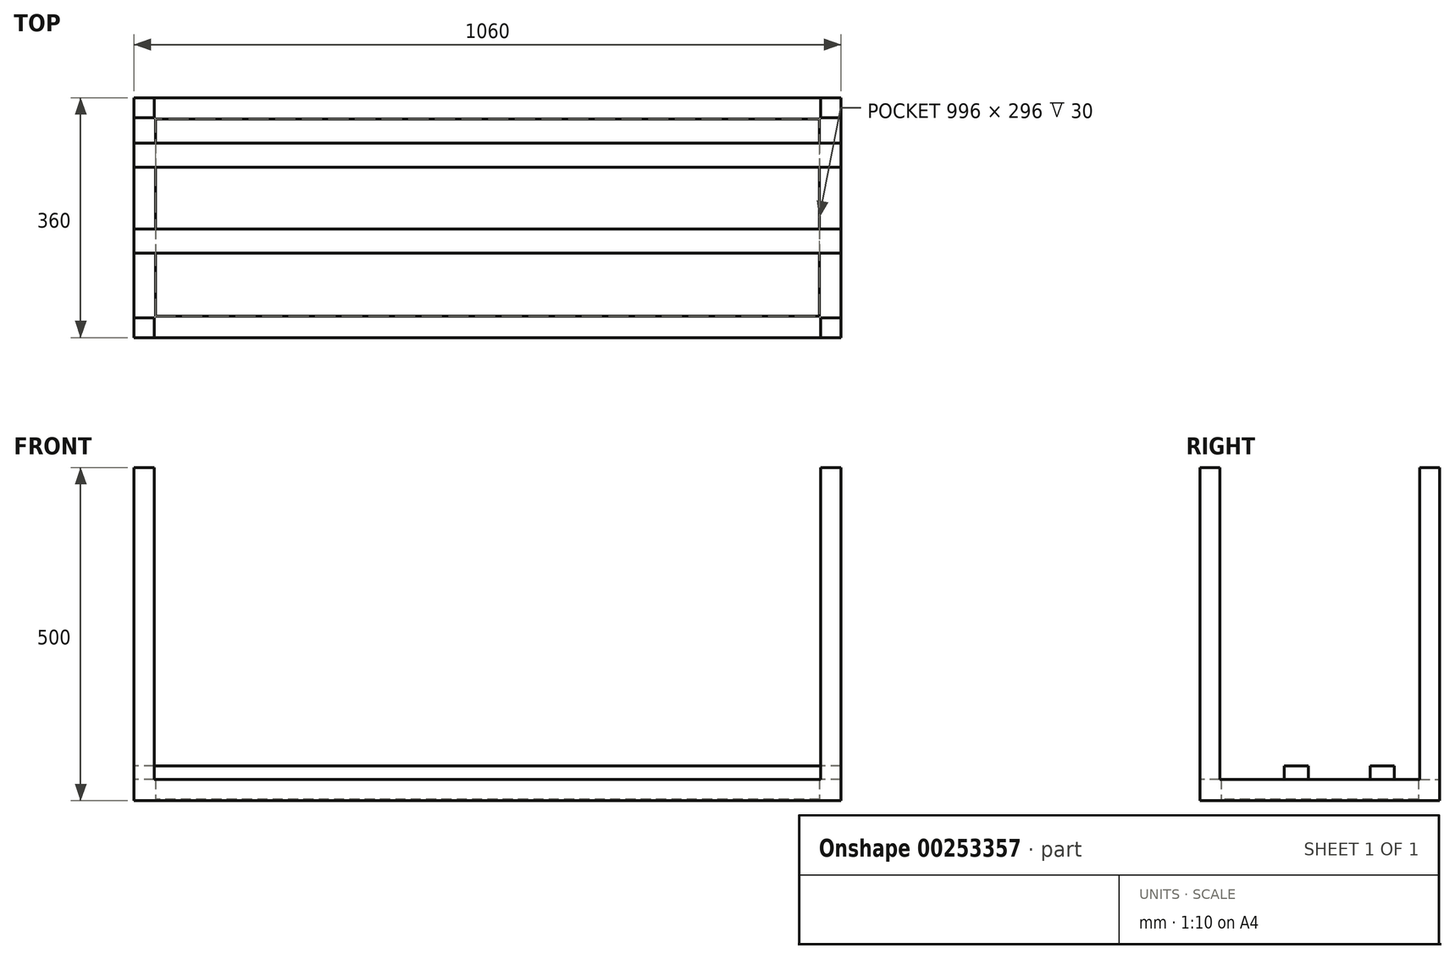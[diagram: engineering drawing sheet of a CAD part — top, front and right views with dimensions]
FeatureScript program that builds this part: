
annotation { "Feature Type Name" : "Feature", "Feature Type Description" : "" }
export const myFeature = defineFeature(function(context is Context, id is Id, definition is map)
    precondition{}
    {
        {
            var Q0;
            Q0=qCreatedBy(makeId("Top.planeOp"),FACE);
            var sketch = newSketch(context, id + "F0", { "sketchPlane" : qUnion([Q0])});
            skLineSegment(sketch, "E0.bottom", {"start": v(500, 150) * mm, "end": v(-500, 150) * mm});
            skLineSegment(sketch, "E0.top", {"start": v(500, -150) * mm, "end": v(-500, -150) * mm});
            skLineSegment(sketch, "E0.left", {"start": v(500, 150) * mm, "end": v(500, -150) * mm});
            skLineSegment(sketch, "E0.right", {"start": v(-500, 150) * mm, "end": v(-500, -150) * mm});
            skPoint(sketch, "E0.middle", {"position": v(0, 0) * mm});
            skLineSegment(sketch, "E1.bottom", {"start": v(530, 180) * mm, "end": v(-530, 180) * mm});
            skLineSegment(sketch, "E1.top", {"start": v(530, -180) * mm, "end": v(-530, -180) * mm});
            skLineSegment(sketch, "E1.left", {"start": v(530, 180) * mm, "end": v(530, -180) * mm});
            skLineSegment(sketch, "E1.right", {"start": v(-530, 180) * mm, "end": v(-530, -180) * mm});
            skLineSegment(sketch, "E2", {"start": v(-500, 150) * mm, "end": v(-500, 180) * mm});
            skLineSegment(sketch, "E3", {"start": v(-500, 150) * mm, "end": v(-530, 150) * mm});
            skLineSegment(sketch, "E4", {"start": v(-500, -150) * mm, "end": v(-530, -150) * mm});
            skLineSegment(sketch, "E5", {"start": v(-500, -150) * mm, "end": v(-500, -180) * mm});
            skLineSegment(sketch, "E6", {"start": v(500, -150) * mm, "end": v(500, -180) * mm});
            skLineSegment(sketch, "E7", {"start": v(500, -150) * mm, "end": v(530, -150) * mm});
            skLineSegment(sketch, "E8", {"start": v(500, 150) * mm, "end": v(500, 180) * mm});
            skLineSegment(sketch, "E9", {"start": v(500, 150) * mm, "end": v(530, 150) * mm});
            skSolve(sketch);
        }
        {
            var Q0;
            Q0=makeQuery(id+"F0.imprint","IMPRINT",FACE,{"disambiguationData":[TD([[makeQuery(id+"F0.imprint","IMPRINT",EDGE,{"derivedFrom":sQuery(id+"F0.wireOp",EDGE,"E0.bottom")}),-1.0]])]});
            var Q1;
            Q1=makeQuery(id+"F0.imprint","IMPRINT",FACE,{"disambiguationData":[TD([[makeQuery(id+"F0.imprint","IMPRINT",EDGE,{"derivedFrom":sQuery(id+"F0.wireOp",EDGE,"E0.right")}),-1.0]])]});
            var Q2;
            Q2=makeQuery(id+"F0.imprint","IMPRINT",FACE,{"disambiguationData":[TD([[makeQuery(id+"F0.imprint","IMPRINT",EDGE,{"derivedFrom":sQuery(id+"F0.wireOp",EDGE,"E0.top")}),1.0]])]});
            var Q3;
            Q3=makeQuery(id+"F0.imprint","IMPRINT",FACE,{"disambiguationData":[TD([[makeQuery(id+"F0.imprint","IMPRINT",EDGE,{"derivedFrom":sQuery(id+"F0.wireOp",EDGE,"E0.left")}),1.0]])]});
            extrude(context, id + "F1", {"entities" : qUnion([Q0, Q1, Q2, Q3]), "depth" : 30 * mm});
        }
        {
            var Q0;
            {var subQ3=sQuery(id+"F0.wireOp",EDGE,"E2");Q0=makeQuery(id+"F0.imprint","IMPRINT",FACE,{"disambiguationData":[TD([[makeQuery(id+"F0.imprint","IMPRINT",EDGE,{"derivedFrom":subQ3}),1.0]])]});}
            var Q1;
            {var subQ4=sQuery(id+"F0.wireOp",EDGE,"E4");Q1=makeQuery(id+"F0.imprint","IMPRINT",FACE,{"disambiguationData":[TD([[makeQuery(id+"F0.imprint","IMPRINT",EDGE,{"derivedFrom":subQ4}),1.0]])]});}
            var Q2;
            {var subQ3=sQuery(id+"F0.wireOp",EDGE,"E6");Q2=makeQuery(id+"F0.imprint","IMPRINT",FACE,{"disambiguationData":[TD([[makeQuery(id+"F0.imprint","IMPRINT",EDGE,{"derivedFrom":subQ3}),1.0]])]});}
            var Q3;
            {var subQ3=sQuery(id+"F0.wireOp",EDGE,"E8");Q3=makeQuery(id+"F0.imprint","IMPRINT",FACE,{"disambiguationData":[TD([[makeQuery(id+"F0.imprint","IMPRINT",EDGE,{"derivedFrom":subQ3}),-1.0]])]});}
            extrude(context, id + "F2", {"entities" : qUnion([Q0, Q1, Q2, Q3]), "operationType" : NewBodyOperationType.ADD, "depth" : 500 * mm});
        }
        {
            var Q0;
            Q0=makeQuery(id+"F0.imprint","IMPRINT",FACE,{"disambiguationData":[TD([[makeQuery(id+"F0.imprint","IMPRINT",EDGE,{"derivedFrom":sQuery(id+"F0.wireOp",EDGE,"E0.bottom")}),1.0]])]});
            extrude(context, id + "F3", {"entities" : qUnion([Q0]), "depth" : 30 * mm});
        }
        {
            var Q0;
            Q0=makeQuery(id+"F3.opExtrude","CAP_FACE",FACE,{"disambiguationData":[OSD([sQuery(id+"F0.wireOp",EDGE,"E0.bottom"),sQuery(id+"F0.wireOp",EDGE,"E0.top"),sQuery(id+"F0.wireOp",EDGE,"E0.left"),sQuery(id+"F0.wireOp",EDGE,"E0.right")])],"isStart":false});
            shell(context, id + "F4", {"entities" : qUnion([Q0]), "thickness" : 2 * mm});
        }
        {
            var Q0;
            Q0=makeQuery(id+"F1.opExtrude","CAP_FACE",FACE,{"disambiguationData":[OSD([sQuery(id+"F0.wireOp",EDGE,"E0.right"),sQuery(id+"F0.wireOp",EDGE,"E1.right"),sQuery(id+"F0.wireOp",EDGE,"E3"),sQuery(id+"F0.wireOp",EDGE,"E4")])],"isStart":false});
            var sketch = newSketch(context, id + "F5", { "sketchPlane" : qUnion([Q0])});
            skLineSegment(sketch, "E10.0", {"start": v(-498, 148) * mm, "end": v(-498, -148) * mm});
            skLineSegment(sketch, "E10.1", {"start": v(-530, 150) * mm, "end": v(-530, -150) * mm});
            skLineSegment(sketch, "E10.2", {"start": v(500, -180) * mm, "end": v(-500, -180) * mm});
            skLineSegment(sketch, "E10.3", {"start": v(-500, -150) * mm, "end": v(-530, -150) * mm});
            skLineSegment(sketch, "E10.4", {"start": v(-500, -150) * mm, "end": v(-500, -180) * mm});
            skLineSegment(sketch, "E10.5", {"start": v(498, -148) * mm, "end": v(-498, -148) * mm});
            skLineSegment(sketch, "E10.6", {"start": v(500, -150) * mm, "end": v(500, -180) * mm});
            skLineSegment(sketch, "E10.7", {"start": v(500, -150) * mm, "end": v(530, -150) * mm});
            skLineSegment(sketch, "E10.8", {"start": v(498, 148) * mm, "end": v(498, -148) * mm});
            skLineSegment(sketch, "E10.9", {"start": v(530, 150) * mm, "end": v(530, -150) * mm});
            skLineSegment(sketch, "E10.10", {"start": v(500, 150) * mm, "end": v(530, 150) * mm});
            skLineSegment(sketch, "E10.11", {"start": v(500, 150) * mm, "end": v(500, 180) * mm});
            skLineSegment(sketch, "E10.12", {"start": v(500, 180) * mm, "end": v(-500, 180) * mm});
            skLineSegment(sketch, "E10.13", {"start": v(498, 148) * mm, "end": v(-498, 148) * mm});
            skLineSegment(sketch, "E10.14", {"start": v(-500, 150) * mm, "end": v(-500, 180) * mm});
            skLineSegment(sketch, "E10.15", {"start": v(-500, 150) * mm, "end": v(-530, 150) * mm});
            skSolve(sketch);
        }
        {
            var Q0;
            Q0=makeQuery(id+"F5.imprint","IMPRINT",FACE,{"disambiguationData":[TD([[makeQuery(id+"F5.imprint","IMPRINT",EDGE,{"derivedFrom":sQuery(id+"F5.wireOp",EDGE,"E10.1")}),1.0]])]});
            var Q1;
            Q1=makeQuery(id+"F5.imprint","IMPRINT",FACE,{"disambiguationData":[TD([[makeQuery(id+"F5.imprint","IMPRINT",EDGE,{"derivedFrom":sQuery(id+"F5.wireOp",EDGE,"E10.0")}),-1.0]])]});
            extrude(context, id + "F6", {"entities" : qUnion([Q0, Q1]), "operationType" : NewBodyOperationType.ADD, "depth" : 2 * mm});
        }
        {
            var Q0;
            Q0=makeQuery(id+"F6.opExtrude","CAP_FACE",FACE,{"disambiguationData":[OSD([sQuery(id+"F5.wireOp",EDGE,"E10.0"),sQuery(id+"F5.wireOp",EDGE,"E10.1"),sQuery(id+"F5.wireOp",EDGE,"E10.2"),sQuery(id+"F5.wireOp",EDGE,"E10.3"),sQuery(id+"F5.wireOp",EDGE,"E10.4"),sQuery(id+"F5.wireOp",EDGE,"E10.5"),sQuery(id+"F5.wireOp",EDGE,"E10.6"),sQuery(id+"F5.wireOp",EDGE,"E10.7"),sQuery(id+"F5.wireOp",EDGE,"E10.8"),sQuery(id+"F5.wireOp",EDGE,"E10.9"),sQuery(id+"F5.wireOp",EDGE,"E10.10"),sQuery(id+"F5.wireOp",EDGE,"E10.11"),sQuery(id+"F5.wireOp",EDGE,"E10.12"),sQuery(id+"F5.wireOp",EDGE,"E10.13"),sQuery(id+"F5.wireOp",EDGE,"E10.14"),sQuery(id+"F5.wireOp",EDGE,"E10.15")])],"isStart":false});
            var sketch = newSketch(context, id + "F7", { "sketchPlane" : qUnion([Q0])});
            skLineSegment(sketch, "E11.bottom", {"start": v(-530, 111.96) * mm, "end": v(530, 111.96) * mm});
            skLineSegment(sketch, "E11.top", {"start": v(-530, 75.77) * mm, "end": v(530, 75.77) * mm});
            skLineSegment(sketch, "E11.left", {"start": v(-530, 111.96) * mm, "end": v(-530, 75.77) * mm});
            skLineSegment(sketch, "E11.right", {"start": v(530, 111.96) * mm, "end": v(530, 75.77) * mm});
            skLineSegment(sketch, "E12.bottom", {"start": v(530, -17.12) * mm, "end": v(-530, -17.12) * mm});
            skLineSegment(sketch, "E12.top", {"start": v(530, -53.03) * mm, "end": v(-530, -53.03) * mm});
            skLineSegment(sketch, "E12.left", {"start": v(530, -17.12) * mm, "end": v(530, -53.03) * mm});
            skLineSegment(sketch, "E12.right", {"start": v(-530, -17.12) * mm, "end": v(-530, -53.03) * mm});
            skSolve(sketch);
        }
        {
            var Q0;
            Q0 = qSketchRegion(id + "F7", true);
            extrude(context, id + "F8", {"entities" : qUnion([Q0]), "depth" : 20 * mm});
        }
    });
